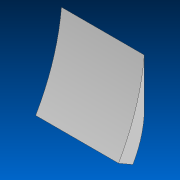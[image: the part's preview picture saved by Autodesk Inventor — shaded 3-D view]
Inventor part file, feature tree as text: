
AUTODESK INVENTOR PART (.ipt)
format: ipt  version: 2022 (Build 260153000, 153)  size: 92,672 bytes
history: native  units: in
note: dims shown in document units (in); Inventor stores cm internally (conversion verified against a paired STEP export)
features: extrude x1, sketch x1
ambient origin geometry x8: Origin, YZ Plane, XZ Plane, XY Plane, X Axis, Y Axis, Z Axis, Center Point
bodies: Solid1 (feature_tree)
feature tree (2):
  extrude  "Extrusion1"  Depth=5.0in
  sketch  "Sketch1"  dims[d0=3.0in d1=1.0in d2=60.0deg d3=1.625in d4=1.5in d5=5.7814in d6=0.817in d7=9.0in d8=3.5in d9=5.0in d10=0.0in]
